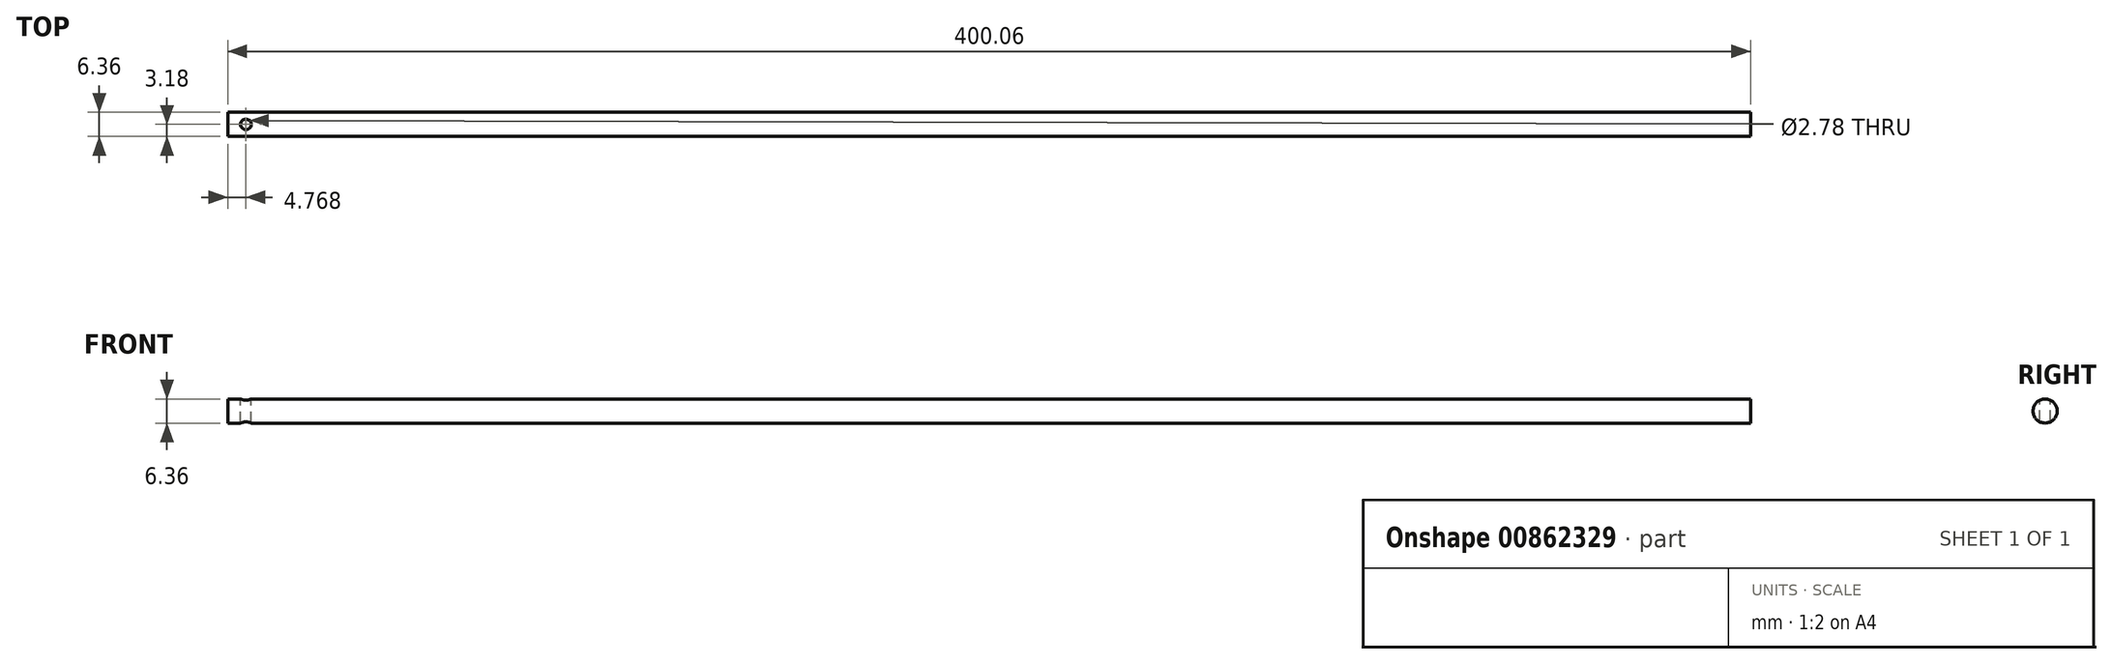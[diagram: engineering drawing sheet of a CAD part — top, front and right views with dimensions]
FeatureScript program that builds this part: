
annotation { "Feature Type Name" : "Feature", "Feature Type Description" : "" }
export const myFeature = defineFeature(function(context is Context, id is Id, definition is map)
    precondition{}
    {
        {
            var Q0;
            Q0=qCreatedBy(makeId("Right.planeOp"),FACE);
            var sketch = newSketch(context, id + "F0", { "sketchPlane" : qUnion([Q0])});
            skCircle(sketch, "E0", {"center": v(0, 0) * mm, "radius": 3.18 * mm});
            skSolve(sketch);
        }
        {
            var Q0;
            Q0 = qSketchRegion(id + "F0", true);
            extrude(context, id + "F1", {"entities" : qUnion([Q0]), "endBound" : BoundingType.SYMMETRIC, "depth" : 400.05 * mm, "offsetDistance" : 25.4 * mm});
        }
        {
            var Q0;
            Q0=qCreatedBy(makeId("Top.planeOp"),FACE);
            var sketch = newSketch(context, id + "F2", { "sketchPlane" : qUnion([Q0])});
            skCircle(sketch, "E1", {"center": v(-195.26, 0) * mm, "radius": 1.39 * mm});
            skSolve(sketch);
        }
        {
            var Q0;
            Q0 = qSketchRegion(id + "F2", true);
            extrude(context, id + "F3", {"entities" : qUnion([Q0]), "operationType" : NewBodyOperationType.REMOVE, "endBound" : BoundingType.UP_TO_NEXT, "oppositeDirection" : true, "depth" : 25.4 * mm, "offsetDistance" : 25.4 * mm, "hasSecondDirection" : true, "secondDirectionBound" : SecondDirectionBoundingType.UP_TO_NEXT, "secondDirectionOppositeDirection" : false, "secondDirectionDepth" : 25.4 * mm});
        }
    });
